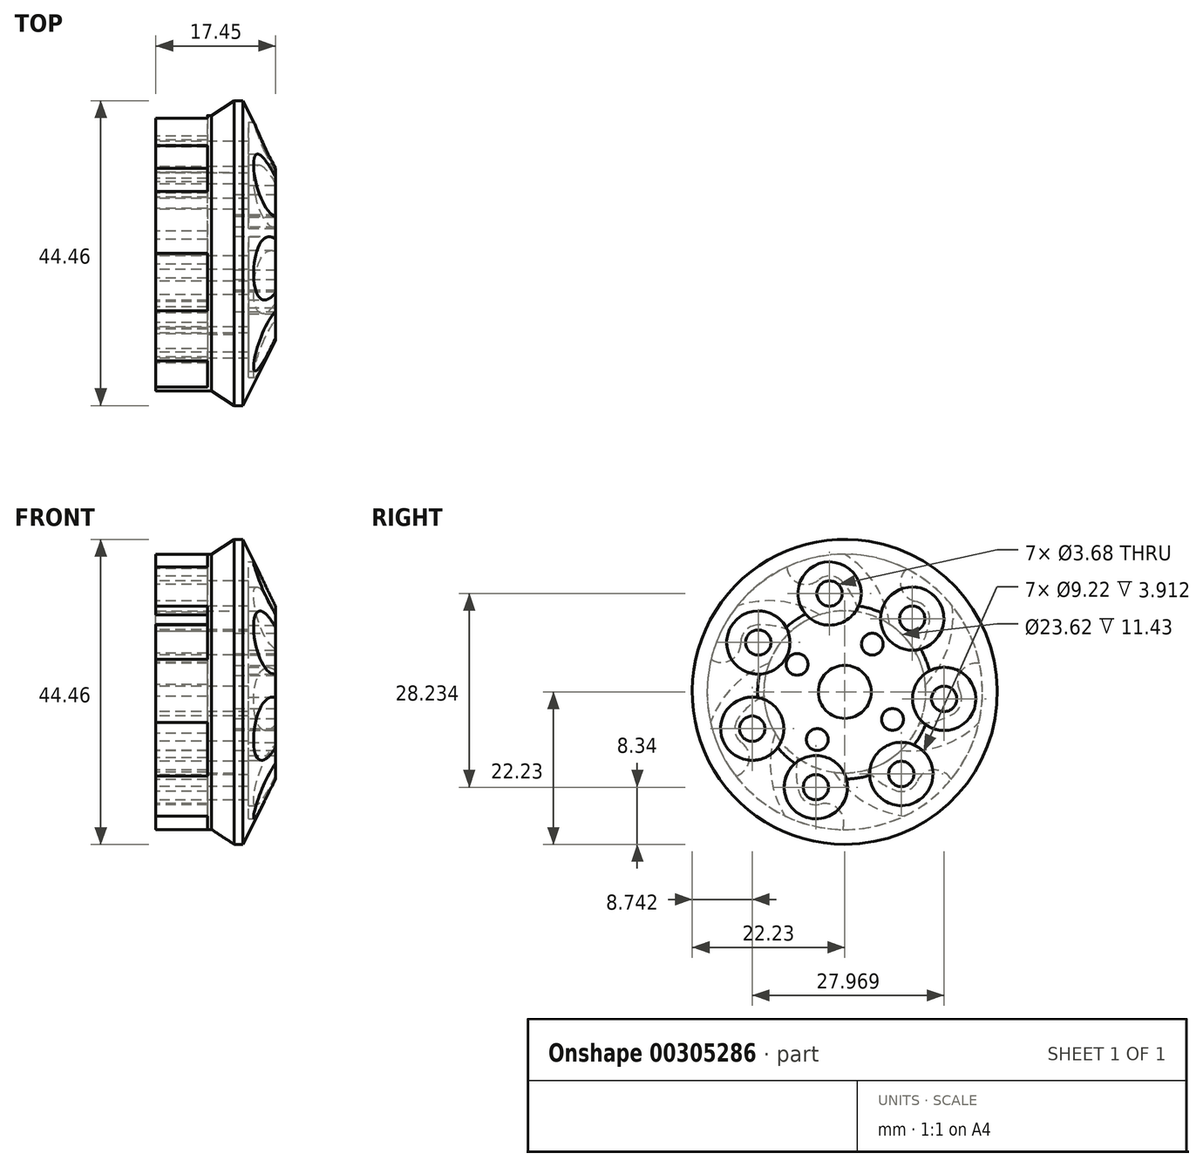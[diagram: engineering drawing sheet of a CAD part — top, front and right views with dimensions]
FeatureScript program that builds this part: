
annotation { "Feature Type Name" : "Feature", "Feature Type Description" : "" }
export const myFeature = defineFeature(function(context is Context, id is Id, definition is map)
    precondition{}
    {
        {
            var Q0;
            Q0=qCreatedBy(makeId("Top.planeOp"),FACE);
            var sketch = newSketch(context, id + "F0", { "sketchPlane" : qUnion([Q0])});
            skLineSegment(sketch, "E0", {"start": v(17.45, 0) * mm, "end": v(17.45, -12.7) * mm});
            skLineSegment(sketch, "E1", {"start": v(17.45, -12.7) * mm, "end": v(12.7, -22.23) * mm});
            skLineSegment(sketch, "E2", {"start": v(12.7, -22.23) * mm, "end": v(11.43, -22.23) * mm});
            skLineSegment(sketch, "E3", {"start": v(11.43, -22.23) * mm, "end": v(8.13, -20.07) * mm});
            skLineSegment(sketch, "E4", {"start": v(8.13, -20.07) * mm, "end": v(0, -20.07) * mm});
            skLineSegment(sketch, "E5", {"start": v(0, -20.07) * mm, "end": v(0, -11.81) * mm});
            skLineSegment(sketch, "E6", {"start": v(0, -11.81) * mm, "end": v(11.43, -11.81) * mm});
            skLineSegment(sketch, "E7", {"start": v(11.43, -11.81) * mm, "end": v(11.43, 0) * mm});
            skLineSegment(sketch, "E8", {"start": v(11.43, 0) * mm, "end": v(17.45, 0) * mm});
            skLineSegment(sketch, "E9", {"start": v(40.63, 0) * mm, "end": v(0, 0) * mm, "construction": true});
            skSolve(sketch);
        }
        {
            var Q0;
            Q0 = qSketchRegion(id + "F0", true);
            var Q1;
            Q1=sQuery(id+"F0.wireOp",EDGE,"E9");
            revolve(context, id + "F1", {"entities" : qUnion([Q0]), "axis" : qUnion([Q1]), "revolveType" : RevolveType.FULL});
        }
        {
            var Q0;
            Q0=qCreatedBy(makeId("Right.planeOp"),FACE);
            var sketch = newSketch(context, id + "F2", { "sketchPlane" : qUnion([Q0])});
            skCircle(sketch, "E10.cCircle", {"center": v(0, 0) * mm, "radius": 20.07 * mm, "construction": true});
            skLineSegment(sketch, "E10.0", {"start": v(-9.66, 20.07) * mm, "end": v(9.66, 20.07) * mm, "construction": true});
            skLineSegment(sketch, "E10.1", {"start": v(9.66, 20.07) * mm, "end": v(21.71, 4.96) * mm, "construction": true});
            skLineSegment(sketch, "E10.2", {"start": v(21.71, 4.96) * mm, "end": v(17.41, -13.89) * mm, "construction": true});
            skLineSegment(sketch, "E10.3", {"start": v(17.41, -13.89) * mm, "end": v(0, -22.27) * mm, "construction": true});
            skLineSegment(sketch, "E10.4", {"start": v(0, -22.27) * mm, "end": v(-17.41, -13.89) * mm, "construction": true});
            skLineSegment(sketch, "E10.5", {"start": v(-17.41, -13.89) * mm, "end": v(-21.71, 4.96) * mm, "construction": true});
            skLineSegment(sketch, "E10.6", {"start": v(-21.71, 4.96) * mm, "end": v(-9.66, 20.07) * mm, "construction": true});
            skPoint(sketch, "E10.0.midPoint", {"position": v(0, 20.07) * mm});
            skLineSegment(sketch, "E11", {"start": v(0, 0) * mm, "end": v(0, 20.07) * mm, "construction": true});
            skLineSegment(sketch, "E12", {"start": v(0, 0) * mm, "end": v(-8.43, 18.2) * mm, "construction": true});
            skLineSegment(sketch, "E13", {"start": v(0, 0) * mm, "end": v(2.02, 11.64) * mm, "construction": true});
            skCircle(sketch, "E14", {"center": v(0, 0) * mm, "radius": 11.81 * mm, "construction": true});
            skPoint(sketch, "E15", {"position": v(0, 11.81) * mm});
            skLineSegment(sketch, "E16", {"start": v(0, 0) * mm, "end": v(6.5, 9.86) * mm, "construction": true});
            skArc(sketch, "E17", {"start": v(6.5, 9.86) * mm, "mid": v(4.4, 15.68) * mm, "end": v(0, 20.07) * mm});
            skCircle(sketch, "E18", {"center": v(0, 0) * mm, "radius": 14.52 * mm, "construction": true});
            skLineSegment(sketch, "E19", {"start": v(0, 0) * mm, "end": v(-2.23, 14.34) * mm, "construction": true});
            skPoint(sketch, "E20", {"position": v(0, 14.52) * mm});
            skCircle(sketch, "E21", {"center": v(-2.23, 14.34) * mm, "radius": 1.84 * mm, "construction": true});
            skArc(sketch, "E22", {"start": v(-0.35, 16.07) * mm, "mid": v(-2.06, 16.9) * mm, "end": v(-3.86, 16.3) * mm});
            skArc(sketch, "E23", {"start": v(2.02, 11.64) * mm, "mid": v(1.12, 14) * mm, "end": v(-0.35, 16.07) * mm});
            skArc(sketch, "E24", {"start": v(-8.43, 18.2) * mm, "mid": v(-6.72, 15.87) * mm, "end": v(-3.86, 16.3) * mm});
            skArc(sketch, "E25", {"start": v(0, 20.07) * mm, "mid": v(-4.73, 21.48) * mm, "end": v(-8.43, 18.2) * mm});
            skArc(sketch, "E26", {"start": v(2.02, 11.64) * mm, "mid": v(4.04, 10.18) * mm, "end": v(6.5, 9.86) * mm});
            skCircle(sketch, "E27", {"center": v(-2.23, 14.34) * mm, "radius": 1.84 * mm});
            skArc(sketch, "E28.1.0", {"start": v(-3.65, 11.23) * mm, "mid": v(-9.53, 13.21) * mm, "end": v(-15.69, 12.51) * mm});
            skArc(sketch, "E28.1.1", {"start": v(-7.84, 8.84) * mm, "mid": v(-5.44, 9.5) * mm, "end": v(-3.65, 11.23) * mm});
            skArc(sketch, "E28.1.2", {"start": v(-7.84, 8.84) * mm, "mid": v(-10.25, 9.6) * mm, "end": v(-12.78, 9.75) * mm});
            skArc(sketch, "E28.1.3", {"start": v(-12.78, 9.75) * mm, "mid": v(-14.49, 8.92) * mm, "end": v(-15.16, 7.15) * mm});
            skArc(sketch, "E28.1.4", {"start": v(-15.69, 12.51) * mm, "mid": v(-19.75, 9.7) * mm, "end": v(-19.5, 4.76) * mm});
            skArc(sketch, "E28.1.5", {"start": v(-19.5, 4.76) * mm, "mid": v(-16.6, 4.64) * mm, "end": v(-15.16, 7.15) * mm});
            skCircle(sketch, "E28.1.6", {"center": v(-12.6, 7.2) * mm, "radius": 1.84 * mm, "construction": true});
            skCircle(sketch, "E28.1.7", {"center": v(-12.6, 7.2) * mm, "radius": 1.84 * mm});
            skArc(sketch, "E28.2.0", {"start": v(-11.06, 4.15) * mm, "mid": v(-16.27, 0.8) * mm, "end": v(-19.56, -4.47) * mm});
            skArc(sketch, "E28.2.1", {"start": v(-11.8, -0.62) * mm, "mid": v(-10.82, 1.68) * mm, "end": v(-11.06, 4.15) * mm});
            skArc(sketch, "E28.2.2", {"start": v(-11.8, -0.62) * mm, "mid": v(-13.9, -2.03) * mm, "end": v(-15.59, -3.91) * mm});
            skArc(sketch, "E28.2.3", {"start": v(-15.59, -3.91) * mm, "mid": v(-16, -5.76) * mm, "end": v(-15.04, -7.4) * mm});
            skArc(sketch, "E28.2.4", {"start": v(-19.56, -4.47) * mm, "mid": v(-19.9, -9.4) * mm, "end": v(-15.87, -12.27) * mm});
            skArc(sketch, "E28.2.5", {"start": v(-15.87, -12.27) * mm, "mid": v(-13.98, -10.09) * mm, "end": v(-15.04, -7.4) * mm});
            skCircle(sketch, "E28.2.6", {"center": v(-13.49, -5.36) * mm, "radius": 1.84 * mm, "construction": true});
            skCircle(sketch, "E28.2.7", {"center": v(-13.49, -5.36) * mm, "radius": 1.84 * mm});
            skArc(sketch, "E28.3.0", {"start": v(-10.14, -6.05) * mm, "mid": v(-10.76, -12.23) * mm, "end": v(-8.7, -18.08) * mm});
            skArc(sketch, "E28.3.1", {"start": v(-6.87, -9.6) * mm, "mid": v(-8.06, -7.42) * mm, "end": v(-10.14, -6.05) * mm});
            skArc(sketch, "E28.3.2", {"start": v(-6.87, -9.6) * mm, "mid": v(-7.08, -12.13) * mm, "end": v(-6.66, -14.63) * mm});
            skArc(sketch, "E28.3.3", {"start": v(-6.66, -14.63) * mm, "mid": v(-5.48, -16.11) * mm, "end": v(-3.6, -16.37) * mm});
            skArc(sketch, "E28.3.4", {"start": v(-8.7, -18.08) * mm, "mid": v(-5.06, -21.41) * mm, "end": v(-0.3, -20.06) * mm});
            skArc(sketch, "E28.3.5", {"start": v(-0.3, -20.06) * mm, "mid": v(-0.83, -17.22) * mm, "end": v(-3.6, -16.37) * mm});
            skCircle(sketch, "E28.3.6", {"center": v(-4.22, -13.9) * mm, "radius": 1.84 * mm, "construction": true});
            skCircle(sketch, "E28.3.7", {"center": v(-4.22, -13.9) * mm, "radius": 1.84 * mm});
            skArc(sketch, "E28.4.0", {"start": v(-1.59, -11.7) * mm, "mid": v(2.85, -16.04) * mm, "end": v(8.7, -18.08) * mm});
            skArc(sketch, "E28.4.1", {"start": v(3.22, -11.36) * mm, "mid": v(0.77, -10.92) * mm, "end": v(-1.59, -11.7) * mm});
            skArc(sketch, "E28.4.2", {"start": v(3.22, -11.36) * mm, "mid": v(5.07, -13.1) * mm, "end": v(7.28, -14.33) * mm});
            skArc(sketch, "E28.4.3", {"start": v(7.28, -14.33) * mm, "mid": v(9.18, -14.33) * mm, "end": v(10.55, -13.01) * mm});
            skArc(sketch, "E28.4.4", {"start": v(8.7, -18.08) * mm, "mid": v(13.59, -17.3) * mm, "end": v(15.5, -12.75) * mm});
            skArc(sketch, "E28.4.5", {"start": v(15.5, -12.75) * mm, "mid": v(12.94, -11.38) * mm, "end": v(10.55, -13.01) * mm});
            skCircle(sketch, "E28.4.6", {"center": v(8.23, -11.96) * mm, "radius": 1.84 * mm, "construction": true});
            skCircle(sketch, "E28.4.7", {"center": v(8.23, -11.96) * mm, "radius": 1.84 * mm});
            skArc(sketch, "E28.5.0", {"start": v(8.16, -8.54) * mm, "mid": v(14.31, -7.77) * mm, "end": v(19.56, -4.47) * mm});
            skArc(sketch, "E28.5.1", {"start": v(10.9, -4.56) * mm, "mid": v(9.02, -6.2) * mm, "end": v(8.16, -8.54) * mm});
            skArc(sketch, "E28.5.2", {"start": v(10.9, -4.56) * mm, "mid": v(13.4, -4.2) * mm, "end": v(15.74, -3.24) * mm});
            skArc(sketch, "E28.5.3", {"start": v(15.74, -3.24) * mm, "mid": v(16.92, -1.75) * mm, "end": v(16.76, 0.14) * mm});
            skArc(sketch, "E28.5.4", {"start": v(19.56, -4.47) * mm, "mid": v(22, -0.17) * mm, "end": v(19.63, 4.17) * mm});
            skArc(sketch, "E28.5.5", {"start": v(19.63, 4.17) * mm, "mid": v(16.97, 3.02) * mm, "end": v(16.76, 0.14) * mm});
            skCircle(sketch, "E28.5.6", {"center": v(14.48, -1.02) * mm, "radius": 1.84 * mm, "construction": true});
            skCircle(sketch, "E28.5.7", {"center": v(14.48, -1.02) * mm, "radius": 1.84 * mm});
            skArc(sketch, "E28.6.0", {"start": v(11.76, 1.06) * mm, "mid": v(15, 6.35) * mm, "end": v(15.69, 12.51) * mm});
            skArc(sketch, "E28.6.1", {"start": v(10.36, 5.67) * mm, "mid": v(10.48, 3.19) * mm, "end": v(11.76, 1.06) * mm});
            skArc(sketch, "E28.6.2", {"start": v(10.36, 5.67) * mm, "mid": v(11.64, 7.86) * mm, "end": v(12.35, 10.29) * mm});
            skArc(sketch, "E28.6.3", {"start": v(12.35, 10.29) * mm, "mid": v(11.92, 12.14) * mm, "end": v(10.34, 13.19) * mm});
            skArc(sketch, "E28.6.4", {"start": v(15.69, 12.51) * mm, "mid": v(13.85, 17.1) * mm, "end": v(8.98, 17.95) * mm});
            skArc(sketch, "E28.6.5", {"start": v(8.98, 17.95) * mm, "mid": v(8.22, 15.15) * mm, "end": v(10.34, 13.19) * mm});
            skCircle(sketch, "E28.6.6", {"center": v(9.83, 10.69) * mm, "radius": 1.84 * mm, "construction": true});
            skCircle(sketch, "E28.6.7", {"center": v(9.83, 10.69) * mm, "radius": 1.84 * mm});
            skSolve(sketch);
        }
        {
            var Q0;
            Q0 = qSketchRegion(id + "F2", true);
            extrude(context, id + "F3", {"entities" : qUnion([Q0]), "operationType" : NewBodyOperationType.REMOVE, "depth" : 7.52 * mm});
        }
        {
            var Q0;
            Q0=qCreatedBy(makeId("Right.planeOp"),FACE);
            var sketch = newSketch(context, id + "F4", { "sketchPlane" : qUnion([Q0])});
            skCircle(sketch, "E29", {"center": v(9.83, 10.69) * mm, "radius": 1.84 * mm});
            skCircle(sketch, "E30.1.0", {"center": v(-2.23, 14.34) * mm, "radius": 1.84 * mm});
            skCircle(sketch, "E30.2.0", {"center": v(-12.6, 7.2) * mm, "radius": 1.84 * mm});
            skCircle(sketch, "E30.3.0", {"center": v(-13.49, -5.36) * mm, "radius": 1.84 * mm});
            skCircle(sketch, "E30.4.0", {"center": v(-4.22, -13.9) * mm, "radius": 1.84 * mm});
            skCircle(sketch, "E30.5.0", {"center": v(8.23, -11.96) * mm, "radius": 1.84 * mm});
            skCircle(sketch, "E30.6.0", {"center": v(14.48, -1.02) * mm, "radius": 1.84 * mm});
            skPoint(sketch, "E30.center", {"position": v(0, 0) * mm});
            skSolve(sketch);
        }
        {
            var Q0;
            Q0=makeQuery(id+"F4.imprint","IMPRINT",FACE,{"disambiguationData":[TD([[makeQuery(id+"F4.imprint","IMPRINT",EDGE,{"derivedFrom":sQuery(id+"F4.wireOp",EDGE,"E29")}),1.0]])]});
            var Q1;
            Q1=makeQuery(id+"F4.imprint","IMPRINT",FACE,{"disambiguationData":[TD([[makeQuery(id+"F4.imprint","IMPRINT",EDGE,{"derivedFrom":sQuery(id+"F4.wireOp",EDGE,"E30.1.0")}),1.0]])]});
            var Q2;
            Q2=makeQuery(id+"F4.imprint","IMPRINT",FACE,{"disambiguationData":[TD([[makeQuery(id+"F4.imprint","IMPRINT",EDGE,{"derivedFrom":sQuery(id+"F4.wireOp",EDGE,"E30.2.0")}),1.0]])]});
            var Q3;
            Q3=makeQuery(id+"F4.imprint","IMPRINT",FACE,{"disambiguationData":[TD([[makeQuery(id+"F4.imprint","IMPRINT",EDGE,{"derivedFrom":sQuery(id+"F4.wireOp",EDGE,"E30.3.0")}),1.0]])]});
            var Q4;
            Q4=makeQuery(id+"F4.imprint","IMPRINT",FACE,{"disambiguationData":[TD([[makeQuery(id+"F4.imprint","IMPRINT",EDGE,{"derivedFrom":sQuery(id+"F4.wireOp",EDGE,"E30.4.0")}),1.0]])]});
            var Q5;
            Q5=makeQuery(id+"F4.imprint","IMPRINT",FACE,{"disambiguationData":[TD([[makeQuery(id+"F4.imprint","IMPRINT",EDGE,{"derivedFrom":sQuery(id+"F4.wireOp",EDGE,"E30.5.0")}),1.0]])]});
            var Q6;
            Q6=makeQuery(id+"F4.imprint","IMPRINT",FACE,{"disambiguationData":[TD([[makeQuery(id+"F4.imprint","IMPRINT",EDGE,{"derivedFrom":sQuery(id+"F4.wireOp",EDGE,"E30.6.0")}),1.0]])]});
            extrude(context, id + "F5", {"entities" : qUnion([Q0, Q1, Q2, Q3, Q4, Q5, Q6]), "operationType" : NewBodyOperationType.REMOVE, "endBound" : BoundingType.THROUGH_ALL, "depth" : 25.4 * mm});
        }
        {
            var Q0;
            Q0=qCreatedBy(makeId("Right.planeOp"),FACE);
            cPlane(context, id + "F6", {"entities" : qUnion([Q0]), "cplaneType" : CPlaneType.OFFSET, "offset" : 17.45 * mm, "width" : 152.4 * mm, "height" : 152.4 * mm});
        }
        {
            var Q0;
            Q0=qCreatedBy(id+"F6.planeOp",FACE);
            var sketch = newSketch(context, id + "F7", { "sketchPlane" : qUnion([Q0])});
            skCircle(sketch, "E31", {"center": v(14.48, -1.02) * mm, "radius": 4.61 * mm});
            skCircle(sketch, "E32.1.0", {"center": v(9.83, 10.69) * mm, "radius": 4.61 * mm});
            skCircle(sketch, "E32.2.0", {"center": v(-2.23, 14.34) * mm, "radius": 4.61 * mm});
            skCircle(sketch, "E32.3.0", {"center": v(-12.6, 7.2) * mm, "radius": 4.61 * mm});
            skCircle(sketch, "E32.4.0", {"center": v(-13.49, -5.36) * mm, "radius": 4.61 * mm});
            skCircle(sketch, "E32.5.0", {"center": v(-4.22, -13.9) * mm, "radius": 4.61 * mm});
            skCircle(sketch, "E32.6.0", {"center": v(8.23, -11.96) * mm, "radius": 4.61 * mm});
            skPoint(sketch, "E32.center", {"position": v(0, 0) * mm});
            skSolve(sketch);
        }
        {
            var Q0;
            Q0 = qSketchRegion(id + "F7", true);
            extrude(context, id + "F8", {"entities" : qUnion([Q0]), "operationType" : NewBodyOperationType.REMOVE, "oppositeDirection" : true, "depth" : 3.91 * mm});
        }
        {
            var Q0;
            Q0=qCreatedBy(id+"F6.planeOp",FACE);
            var sketch = newSketch(context, id + "F9", { "sketchPlane" : qUnion([Q0])});
            skCircle(sketch, "E33", {"center": v(0, 0) * mm, "radius": 3.86 * mm});
            skCircle(sketch, "E34", {"center": v(6.95, -4.01) * mm, "radius": 1.59 * mm});
            skLineSegment(sketch, "E35", {"start": v(0, 0) * mm, "end": v(22.23, 0) * mm, "construction": true});
            skLineSegment(sketch, "E36", {"start": v(0, 0) * mm, "end": v(6.95, -4.01) * mm, "construction": true});
            skCircle(sketch, "E37.1.0", {"center": v(4.01, 6.95) * mm, "radius": 1.59 * mm});
            skCircle(sketch, "E37.2.0", {"center": v(-6.95, 4.01) * mm, "radius": 1.59 * mm});
            skCircle(sketch, "E37.3.0", {"center": v(-4.01, -6.95) * mm, "radius": 1.59 * mm});
            skSolve(sketch);
        }
        {
            var Q0;
            Q0 = qSketchRegion(id + "F9", true);
            extrude(context, id + "F10", {"entities" : qUnion([Q0]), "operationType" : NewBodyOperationType.REMOVE, "endBound" : BoundingType.THROUGH_ALL, "oppositeDirection" : true, "depth" : 25.4 * mm});
        }
    });
